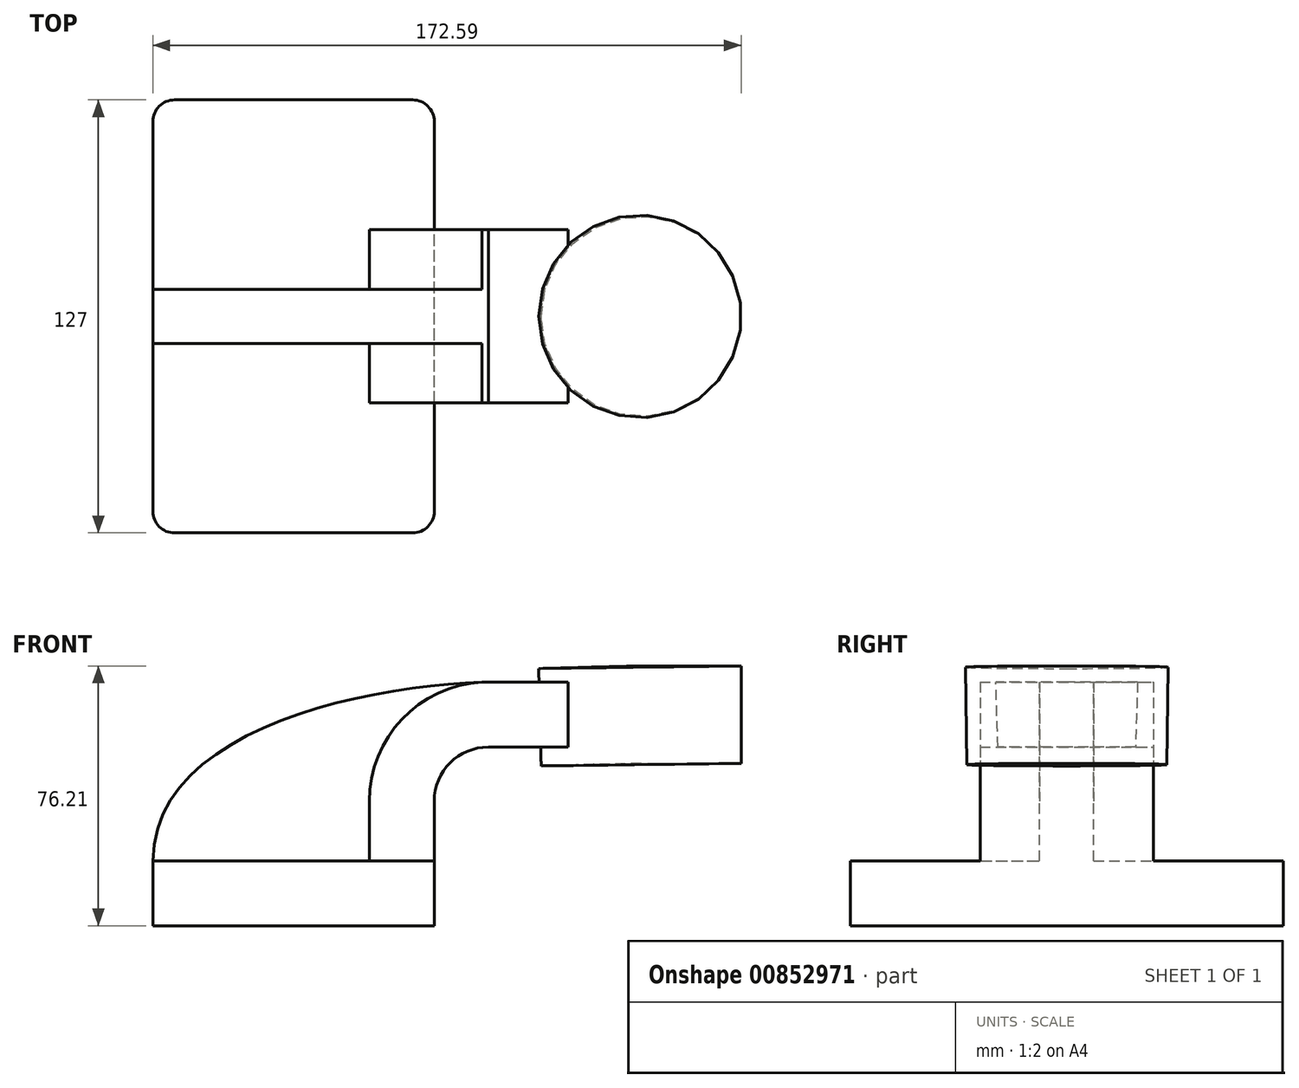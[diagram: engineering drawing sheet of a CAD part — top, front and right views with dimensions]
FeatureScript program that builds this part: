
annotation { "Feature Type Name" : "Feature", "Feature Type Description" : "" }
export const myFeature = defineFeature(function(context is Context, id is Id, definition is map)
    precondition{}
    {
        {
            var Q0;
            Q0=qCreatedBy(makeId("Front.planeOp"),FACE);
            var sketch = newSketch(context, id + "F0", { "sketchPlane" : qUnion([Q0])});
            skLineSegment(sketch, "E0.bottom", {"start": v(-41.28, 9.52) * mm, "end": v(41.27, 9.53) * mm});
            skLineSegment(sketch, "E0.top", {"start": v(-41.28, -9.53) * mm, "end": v(41.28, -9.53) * mm});
            skLineSegment(sketch, "E0.left", {"start": v(-41.28, 9.52) * mm, "end": v(-41.28, -9.53) * mm});
            skLineSegment(sketch, "E0.right", {"start": v(41.27, 9.53) * mm, "end": v(41.28, -9.52) * mm});
            skPoint(sketch, "E0.middle", {"position": v(0, 0) * mm});
            skLineSegment(sketch, "E1.bottom", {"start": v(131.3, 66.68) * mm, "end": v(80.5, 66.68) * mm});
            skLineSegment(sketch, "E1.top", {"start": v(131.3, 38.1) * mm, "end": v(80.5, 38.1) * mm});
            skLineSegment(sketch, "E1.left", {"start": v(131.3, 66.68) * mm, "end": v(131.3, 38.1) * mm});
            skLineSegment(sketch, "E1.right", {"start": v(80.5, 66.68) * mm, "end": v(80.5, 38.1) * mm});
            skPoint(sketch, "E1.middle", {"position": v(105.9, 52.39) * mm});
            skLineSegment(sketch, "E2", {"start": v(41.27, 9.53) * mm, "end": v(41.27, 27) * mm});
            skArc(sketch, "E3", {"start": v(41.27, 27) * mm, "mid": v(45.92, 38.23) * mm, "end": v(57.15, 42.88) * mm});
            skLineSegment(sketch, "E4", {"start": v(57.15, 42.88) * mm, "end": v(101.6, 42.88) * mm});
            skLineSegment(sketch, "E5.0", {"start": v(57.15, 61.93) * mm, "end": v(101.6, 61.93) * mm});
            skArc(sketch, "E5.1", {"start": v(22.22, 27) * mm, "mid": v(32.45, 51.7) * mm, "end": v(57.15, 61.93) * mm});
            skLineSegment(sketch, "E5.2", {"start": v(22.22, 9.53) * mm, "end": v(22.22, 27) * mm});
            skLineSegment(sketch, "E6", {"start": v(101.97, 38.1) * mm, "end": v(101.6, 66.68) * mm});
            skFitSpline(sketch, "E7", {"points": [v(-41.28, 9.53) * mm, v(57.15, 61.93) * mm], "startDerivative": vector(0.56, 116.38) * mm, "endDerivative": vector(106.5, 2.28) * mm});
            skSolve(sketch);
        }
        {
            var Q0;
            Q0=makeQuery(id+"F0.imprint","IMPRINT",FACE,{"disambiguationData":[TD([[makeQuery(id+"F0.imprint","IMPRINT",EDGE,{"derivedFrom":sQuery(id+"F0.wireOp",EDGE,"E0.top")}),1.0]])]});
            extrude(context, id + "F1", {"entities" : qUnion([Q0]), "endBound" : BoundingType.SYMMETRIC, "depth" : 127 * mm, "offsetDistance" : 25.4 * mm});
        }
        {
            var Q0;
            {var subQ1=sQuery(id+"F0.wireOp",EDGE,"E2");Q0=makeQuery(id+"F0.imprint","IMPRINT",FACE,{"disambiguationData":[TD([[makeQuery(id+"F0.imprint","IMPRINT",EDGE,{"derivedFrom":subQ1}),1.0]])]});}
            extrude(context, id + "F2", {"entities" : qUnion([Q0]), "operationType" : NewBodyOperationType.ADD, "endBound" : BoundingType.SYMMETRIC, "depth" : 50.8 * mm, "offsetDistance" : 25.4 * mm});
        }
        {
            var Q0;
            {var subQ3=sQuery(id+"F0.wireOp",EDGE,"E5.2");Q0=makeQuery(id+"F0.imprint","IMPRINT",FACE,{"disambiguationData":[TD([[makeQuery(id+"F0.imprint","IMPRINT",EDGE,{"derivedFrom":subQ3}),1.0]])]});}
            extrude(context, id + "F3", {"entities" : qUnion([Q0]), "operationType" : NewBodyOperationType.ADD, "endBound" : BoundingType.SYMMETRIC, "depth" : 15.88 * mm, "offsetDistance" : 25.4 * mm});
        }
        {
            var Q0;
            {var subQ0=sQuery(id+"F0.wireOp",EDGE,"E1.left");Q0=makeQuery(id+"F0.imprint","IMPRINT",FACE,{"disambiguationData":[TD([[makeQuery(id+"F0.imprint","IMPRINT",EDGE,{"derivedFrom":subQ0}),-1.0]])]});}
            var Q1;
            Q1=sQuery(id+"F0.wireOp",EDGE,"E6");
            revolve(context, id + "F4", {"operationType" : NewBodyOperationType.ADD, "surfaceOperationType" : NewSurfaceOperationType.NEW, "entities" : qUnion([Q0]), "axis" : qUnion([Q1]), "revolveType" : RevolveType.FULL});
        }
        {
            var Q0;
            Q0=makeQuery(id+"F1.opExtrude","CAP_EDGE",EDGE,{"disambiguationData":[OSD([sQuery(id+"F0.wireOp",EDGE,"E0.right")])],"isStart":false});
            var Q1;
            Q1=makeQuery(id+"F1.opExtrude","CAP_EDGE",EDGE,{"disambiguationData":[OSD([sQuery(id+"F0.wireOp",EDGE,"E0.left")])],"isStart":false});
            var Q2;
            Q2=makeQuery(id+"F1.opExtrude","CAP_EDGE",EDGE,{"disambiguationData":[OSD([sQuery(id+"F0.wireOp",EDGE,"E0.left")])],"isStart":true});
            var Q3;
            Q3=makeQuery(id+"F1.opExtrude","CAP_EDGE",EDGE,{"disambiguationData":[OSD([sQuery(id+"F0.wireOp",EDGE,"E0.right")])],"isStart":true});
            fillet(context, id + "F5", {"entities" : qUnion([Q0, Q1, Q2, Q3]), "radius" : 6.35 * mm, "tangentPropagation" : true, "allowEdgeOverflow" : false});
        }
    });
